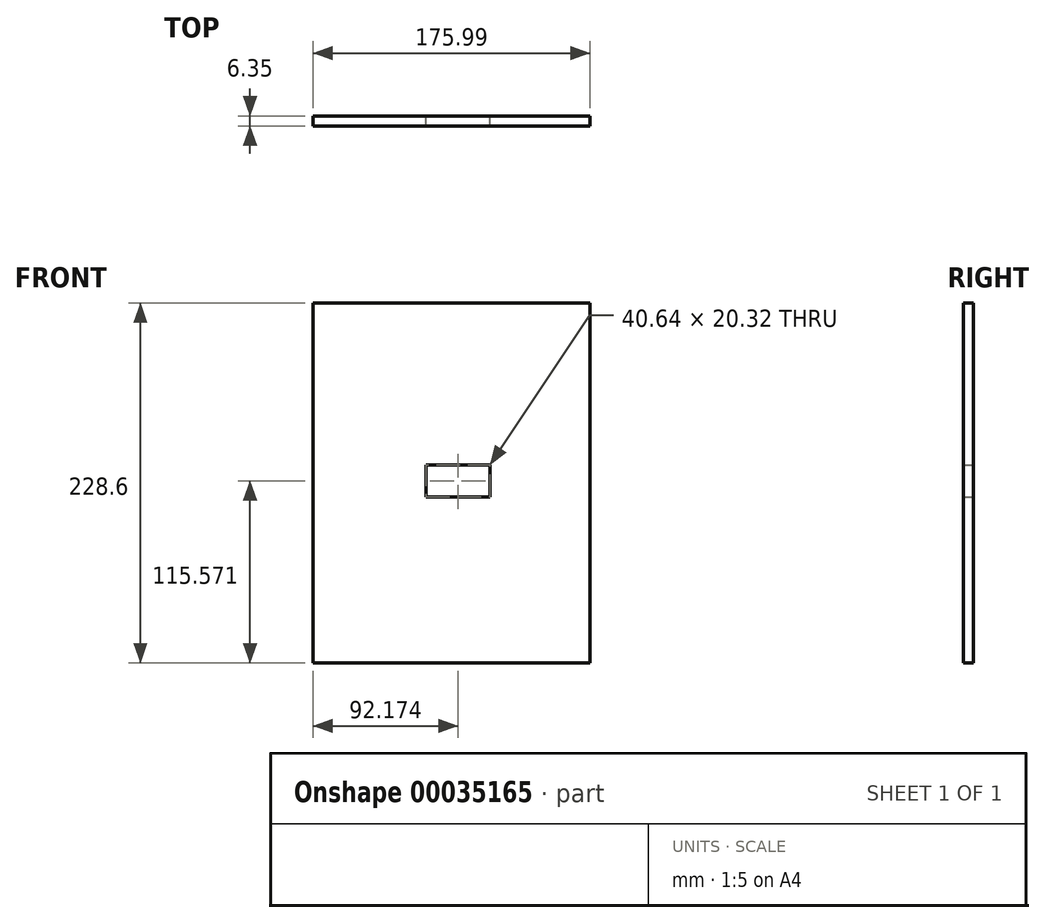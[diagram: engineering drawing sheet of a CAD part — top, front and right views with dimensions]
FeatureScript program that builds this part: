
annotation { "Feature Type Name" : "Feature", "Feature Type Description" : "" }
export const myFeature = defineFeature(function(context is Context, id is Id, definition is map)
    precondition{}
    {
        {
            var Q0;
            Q0=qCreatedBy(makeId("Front.planeOp"),FACE);
            var sketch = newSketch(context, id + "F0", { "sketchPlane" : qUnion([Q0])});
            skLineSegment(sketch, "E0.bottom", {"start": v(-89.57, 118.16) * mm, "end": v(86.42, 118.16) * mm});
            skLineSegment(sketch, "E0.top", {"start": v(-89.57, -110.44) * mm, "end": v(86.42, -110.44) * mm});
            skLineSegment(sketch, "E0.left", {"start": v(-89.57, 118.16) * mm, "end": v(-89.57, -110.44) * mm});
            skLineSegment(sketch, "E0.right", {"start": v(86.42, 118.16) * mm, "end": v(86.42, -110.44) * mm});
            skLineSegment(sketch, "E1.bottom", {"start": v(-17.72, 15.3) * mm, "end": v(22.92, 15.3) * mm});
            skLineSegment(sketch, "E1.top", {"start": v(-17.72, -5.03) * mm, "end": v(22.92, -5.03) * mm});
            skLineSegment(sketch, "E1.left", {"start": v(-17.72, 15.3) * mm, "end": v(-17.72, -5.03) * mm});
            skLineSegment(sketch, "E1.right", {"start": v(22.92, 15.3) * mm, "end": v(22.92, -5.03) * mm});
            skSolve(sketch);
        }
        {
            var Q0;
            Q0=makeQuery(id+"F0.imprint","IMPRINT",FACE,{"disambiguationData":[TD([[makeQuery(id+"F0.imprint","IMPRINT",EDGE,{"derivedFrom":sQuery(id+"F0.wireOp",EDGE,"E0.bottom")}),-1.0]])]});
            extrude(context, id + "F1", {"entities" : qUnion([Q0]), "depth" : 6.35 * mm});
        }
    });
